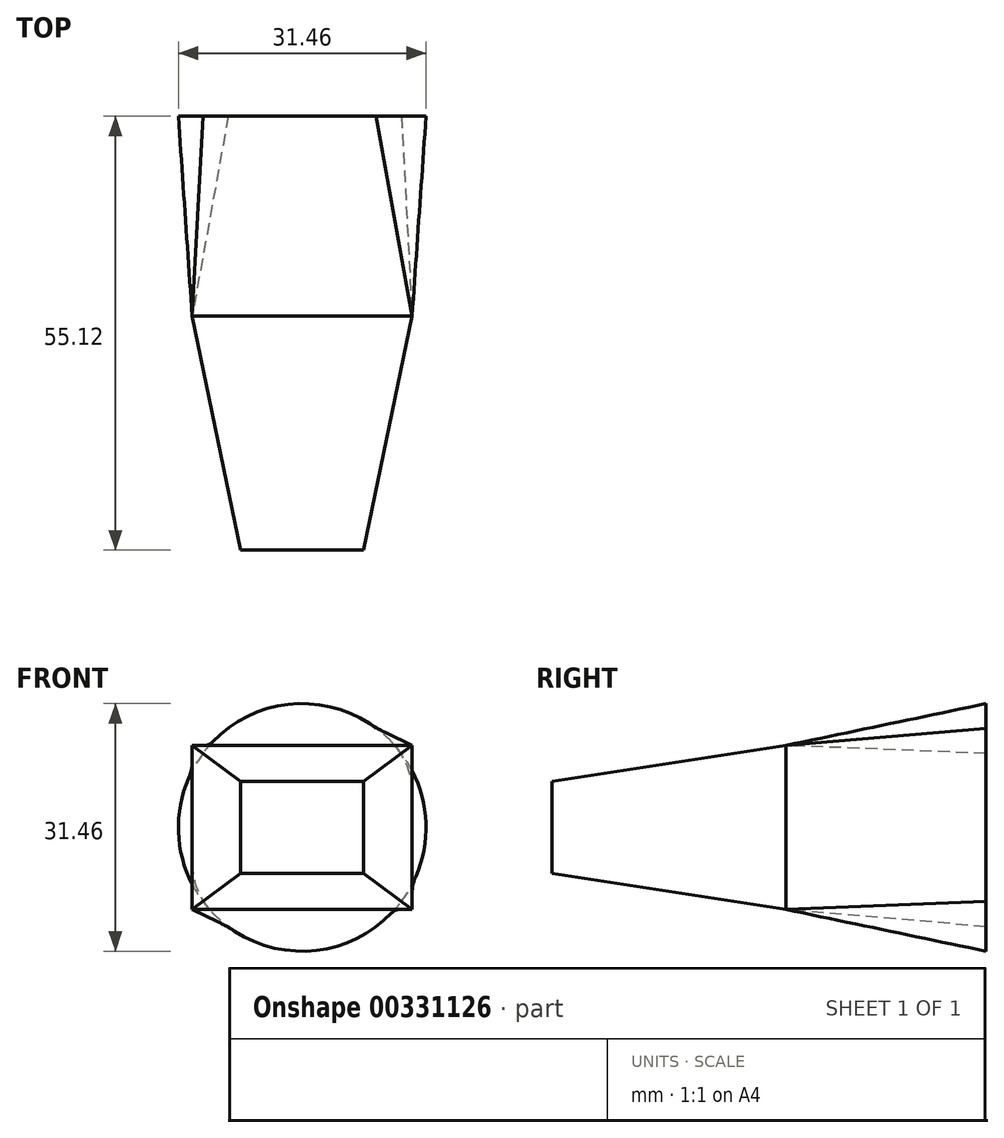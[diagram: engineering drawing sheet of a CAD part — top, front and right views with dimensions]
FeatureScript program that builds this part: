
annotation { "Feature Type Name" : "Feature", "Feature Type Description" : "" }
export const myFeature = defineFeature(function(context is Context, id is Id, definition is map)
    precondition{}
    {
        {
            var Q0;
            Q0=qCreatedBy(makeId("Front.planeOp"),FACE);
            var sketch = newSketch(context, id + "F0", { "sketchPlane" : qUnion([Q0])});
            skCircle(sketch, "E0", {"center": v(0, 0) * mm, "radius": 15.73 * mm});
            skSolve(sketch);
        }
        {
            var Q0;
            Q0=makeQuery(id+"F0.imprint","IMPRINT",FACE,{"disambiguationData":[TD([[makeQuery(id+"F0.imprint","IMPRINT",EDGE,{"derivedFrom":sQuery(id+"F0.wireOp",EDGE,"E0")}),1.0]])]});
            cPlane(context, id + "F1", {"entities" : qUnion([Q0]), "cplaneType" : CPlaneType.OFFSET, "offset" : 25.4 * mm, "width" : 152.4 * mm, "height" : 152.4 * mm});
        }
        {
            var Q0;
            Q0=qCreatedBy(id+"F1.planeOp",FACE);
            var sketch = newSketch(context, id + "F2", { "sketchPlane" : qUnion([Q0])});
            skLineSegment(sketch, "E1.bottom", {"start": v(-13.97, 10.41) * mm, "end": v(13.97, 10.41) * mm});
            skLineSegment(sketch, "E1.top", {"start": v(-13.97, -10.41) * mm, "end": v(13.97, -10.41) * mm});
            skLineSegment(sketch, "E1.left", {"start": v(-13.97, 10.41) * mm, "end": v(-13.97, -10.41) * mm});
            skLineSegment(sketch, "E1.right", {"start": v(13.97, 10.41) * mm, "end": v(13.97, -10.41) * mm});
            skPoint(sketch, "E1.middle", {"position": v(0, 0) * mm});
            skSolve(sketch);
        }
        {
            var Q0;
            Q0=makeQuery(id+"F0.imprint","IMPRINT",FACE,{"disambiguationData":[TD([[makeQuery(id+"F0.imprint","IMPRINT",EDGE,{"derivedFrom":sQuery(id+"F0.wireOp",EDGE,"E0")}),1.0]])]});
            var Q1;
            Q1=makeQuery(id+"F2.imprint","IMPRINT",FACE,{"disambiguationData":[TD([[makeQuery(id+"F2.imprint","IMPRINT",EDGE,{"derivedFrom":sQuery(id+"F2.wireOp",EDGE,"E1.bottom")}),-1.0]])]});
            loft(context, id + "F3", {"sheetProfilesArray" : [{ "sheetProfileEntities" : qUnion([Q0]) }, { "sheetProfileEntities" : qUnion([Q1]) }]});
        }
        {
            var Q0;
            Q0=makeQuery(id+"F3.opLoft","CAP_FACE",FACE,{"disambiguationData":[OSD([makeQuery(id+"F2.imprint","IMPRINT",FACE,{"disambiguationData":[TD([[makeQuery(id+"F2.imprint","IMPRINT",EDGE,{"derivedFrom":sQuery(id+"F2.wireOp",EDGE,"E1.bottom")}),-1.0]])]})])],"isStart":true});
            cPlane(context, id + "F4", {"entities" : qUnion([Q0]), "cplaneType" : CPlaneType.OFFSET, "offset" : 29.72 * mm, "width" : 152.4 * mm, "height" : 152.4 * mm});
        }
        {
            var Q0;
            Q0=qCreatedBy(id+"F4.planeOp",FACE);
            var sketch = newSketch(context, id + "F5", { "sketchPlane" : qUnion([Q0])});
            skLineSegment(sketch, "E2.bottom", {"start": v(-7.8, 5.86) * mm, "end": v(7.8, 5.86) * mm});
            skLineSegment(sketch, "E2.top", {"start": v(-7.8, -5.86) * mm, "end": v(7.8, -5.86) * mm});
            skLineSegment(sketch, "E2.left", {"start": v(-7.8, 5.86) * mm, "end": v(-7.8, -5.86) * mm});
            skLineSegment(sketch, "E2.right", {"start": v(7.8, 5.86) * mm, "end": v(7.8, -5.86) * mm});
            skPoint(sketch, "E2.middle", {"position": v(0, 0) * mm});
            skSolve(sketch);
        }
        {
            var Q1;
            Q1=makeQuery(id+"F3.opLoft","CAP_FACE",FACE,{"disambiguationData":[OSD([makeQuery(id+"F2.imprint","IMPRINT",FACE,{"disambiguationData":[TD([[makeQuery(id+"F2.imprint","IMPRINT",EDGE,{"derivedFrom":sQuery(id+"F2.wireOp",EDGE,"E1.bottom")}),-1.0]])]})])],"isStart":true});
            var Q2;
            Q2=makeQuery(id+"F5.imprint","IMPRINT",FACE,{"disambiguationData":[TD([[makeQuery(id+"F5.imprint","IMPRINT",EDGE,{"derivedFrom":sQuery(id+"F5.wireOp",EDGE,"E2.bottom")}),-1.0]])]});
            loft(context, id + "F6", {"operationType" : NewBodyOperationType.ADD, "sheetProfilesArray" : [{ "sheetProfileEntities" : qUnion([Q1]) }, { "sheetProfileEntities" : qUnion([Q2]) }]});
        }
    });
